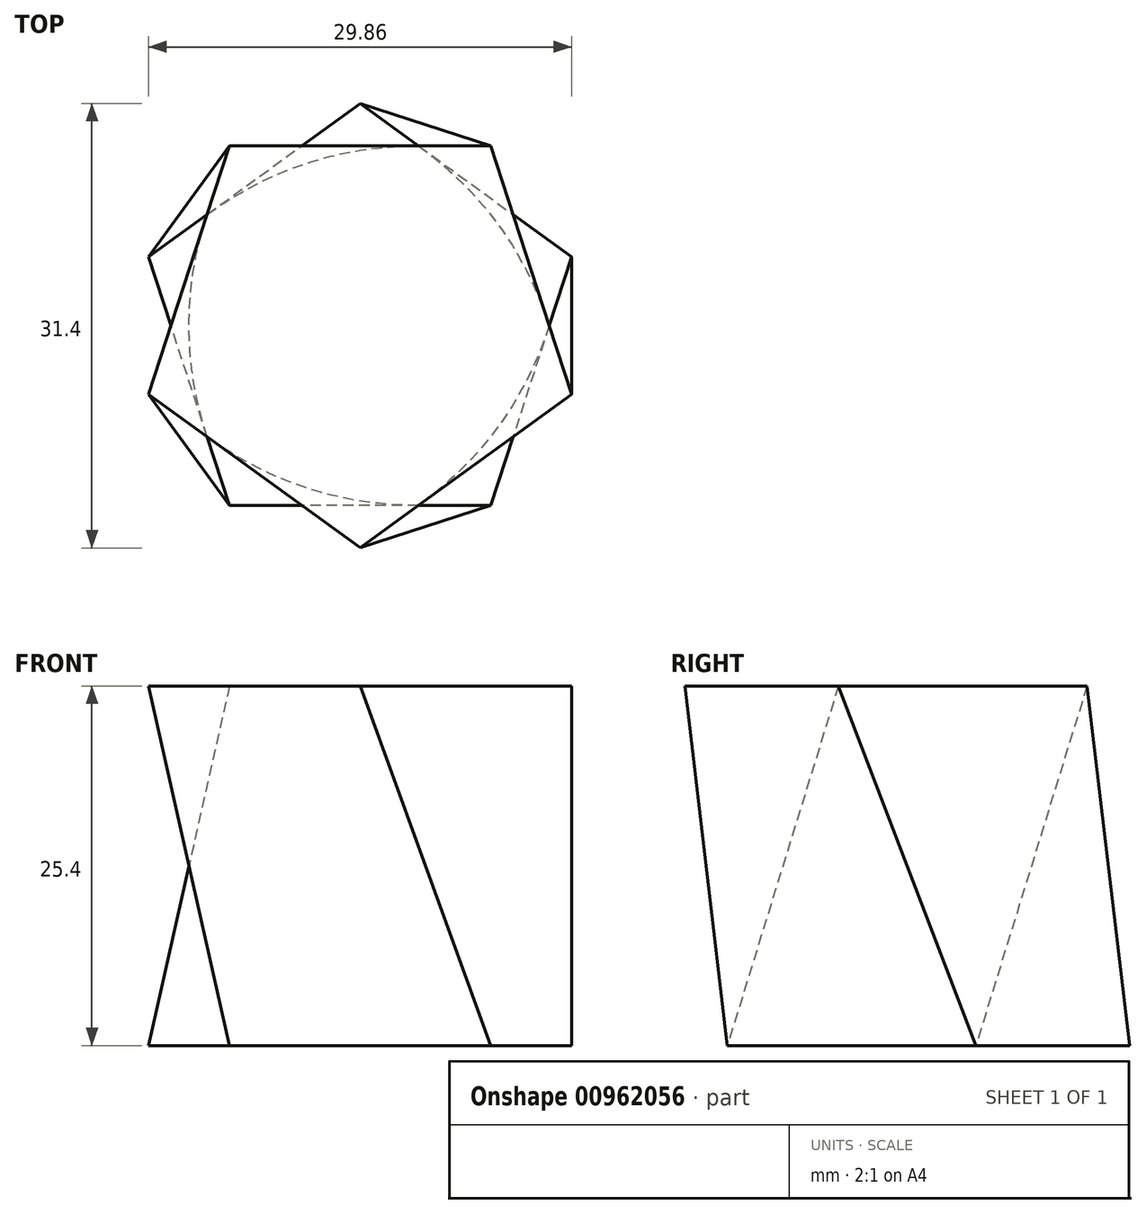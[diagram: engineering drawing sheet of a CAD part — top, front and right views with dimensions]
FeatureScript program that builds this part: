
annotation { "Feature Type Name" : "Feature", "Feature Type Description" : "" }
export const myFeature = defineFeature(function(context is Context, id is Id, definition is map)
    precondition{}
    {
        {
            var Q0;
            Q0=qCreatedBy(makeId("Top.planeOp"),FACE);
            var sketch = newSketch(context, id + "F0", { "sketchPlane" : qUnion([Q0])});
            skCircle(sketch, "E0.cCircle", {"center": v(0, 0) * mm, "radius": 12.7 * mm, "construction": true});
            skLineSegment(sketch, "E0.0", {"start": v(14.93, 4.85) * mm, "end": v(9.23, -12.7) * mm});
            skLineSegment(sketch, "E0.1", {"start": v(9.23, -12.7) * mm, "end": v(-9.23, -12.7) * mm});
            skLineSegment(sketch, "E0.2", {"start": v(-9.23, -12.7) * mm, "end": v(-14.93, 4.85) * mm});
            skLineSegment(sketch, "E0.3", {"start": v(-14.93, 4.85) * mm, "end": v(0, 15.7) * mm});
            skLineSegment(sketch, "E0.4", {"start": v(0, 15.7) * mm, "end": v(14.93, 4.85) * mm});
            skPoint(sketch, "E0.0.midPoint", {"position": v(12.08, -3.92) * mm});
            skSolve(sketch);
        }
        {
            var Q0;
            Q0=qCreatedBy(makeId("Top.planeOp"),FACE);
            cPlane(context, id + "F1", {"entities" : qUnion([Q0]), "cplaneType" : CPlaneType.OFFSET, "offset" : 25.4 * mm, "width" : 152.4 * mm, "height" : 152.4 * mm});
        }
        {
            var Q0;
            Q0=qCreatedBy(id+"F1.planeOp",FACE);
            var sketch = newSketch(context, id + "F2", { "sketchPlane" : qUnion([Q0])});
            skCircle(sketch, "E1.cCircle", {"center": v(0, 0) * mm, "radius": 12.7 * mm, "construction": true});
            skLineSegment(sketch, "E1.0", {"start": v(-9.23, 12.7) * mm, "end": v(9.23, 12.7) * mm});
            skLineSegment(sketch, "E1.1", {"start": v(9.23, 12.7) * mm, "end": v(14.93, -4.85) * mm});
            skLineSegment(sketch, "E1.2", {"start": v(14.93, -4.85) * mm, "end": v(0, -15.7) * mm});
            skLineSegment(sketch, "E1.3", {"start": v(0, -15.7) * mm, "end": v(-14.93, -4.85) * mm});
            skLineSegment(sketch, "E1.4", {"start": v(-14.93, -4.85) * mm, "end": v(-9.23, 12.7) * mm});
            skPoint(sketch, "E1.0.midPoint", {"position": v(0, 12.7) * mm});
            skSolve(sketch);
        }
        {
            var Q0;
            Q0=makeQuery(id+"F2.imprint","IMPRINT",FACE,{"disambiguationData":[TD([[makeQuery(id+"F2.imprint","IMPRINT",EDGE,{"derivedFrom":sQuery(id+"F2.wireOp",EDGE,"E1.0")}),-1.0]])]});
            var Q1;
            Q1=makeQuery(id+"F0.imprint","IMPRINT",FACE,{"disambiguationData":[TD([[makeQuery(id+"F0.imprint","IMPRINT",EDGE,{"derivedFrom":sQuery(id+"F0.wireOp",EDGE,"E0.0")}),-1.0]])]});
            loft(context, id + "F3", {"sheetProfilesArray" : [{ "sheetProfileEntities" : qUnion([Q0]) }, { "sheetProfileEntities" : qUnion([Q1]) }]});
        }
    });
